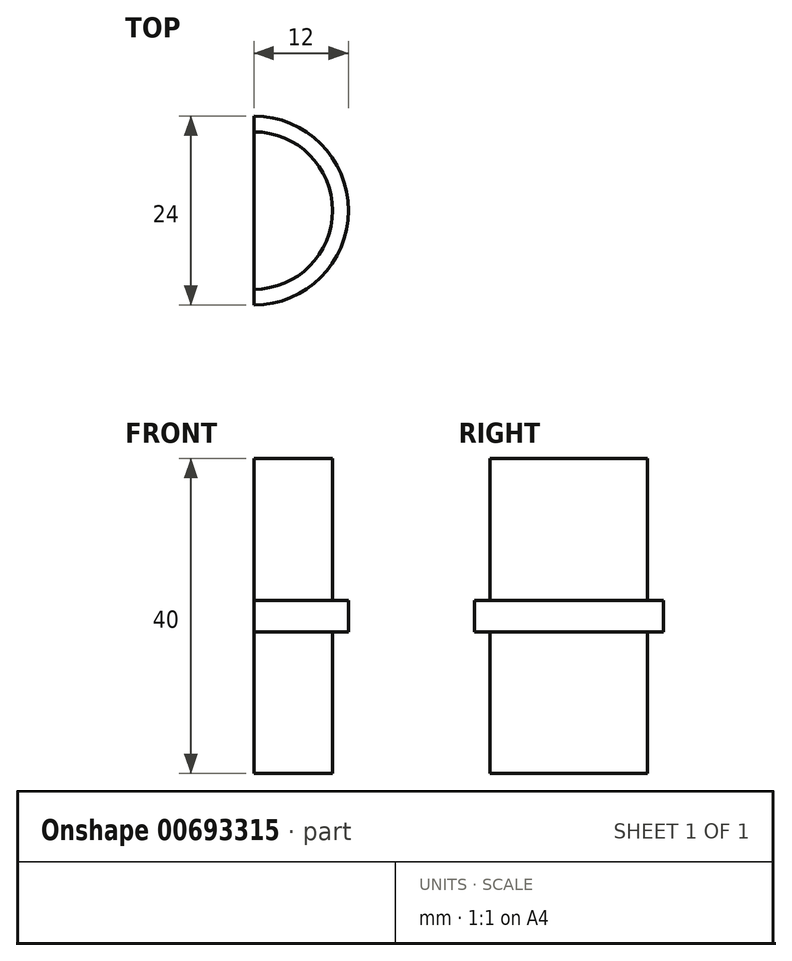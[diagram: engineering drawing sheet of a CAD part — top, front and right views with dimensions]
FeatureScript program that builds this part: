
annotation { "Feature Type Name" : "Feature", "Feature Type Description" : "" }
export const myFeature = defineFeature(function(context is Context, id is Id, definition is map)
    precondition{}
    {
        {
            var Q0;
            Q0=qCreatedBy(makeId("Front.planeOp"),FACE);
            var sketch = newSketch(context, id + "F0", { "sketchPlane" : qUnion([Q0])});
            skLineSegment(sketch, "E0", {"start": v(0, 0) * mm, "end": v(0, 20) * mm});
            skLineSegment(sketch, "E1", {"start": v(0, 20) * mm, "end": v(10, 20) * mm});
            skLineSegment(sketch, "E2", {"start": v(10, 20) * mm, "end": v(10, 0) * mm});
            skLineSegment(sketch, "E3", {"start": v(10, 0) * mm, "end": v(10, -20) * mm});
            skLineSegment(sketch, "E4", {"start": v(10, -20) * mm, "end": v(0, -20) * mm});
            skLineSegment(sketch, "E5", {"start": v(0, -20) * mm, "end": v(0, 0) * mm});
            skLineSegment(sketch, "E6", {"start": v(10, 0) * mm, "end": v(12, 0) * mm});
            skLineSegment(sketch, "E7", {"start": v(12, 0) * mm, "end": v(12, 2) * mm});
            skLineSegment(sketch, "E8", {"start": v(12, 2) * mm, "end": v(10, 2) * mm});
            skLineSegment(sketch, "E9", {"start": v(12, 0) * mm, "end": v(12, -2) * mm});
            skLineSegment(sketch, "E10", {"start": v(12, -2) * mm, "end": v(10, -2) * mm});
            skSolve(sketch);
        }
        {
            var Q0;
            Q0=makeQuery(id+"F0.imprint","IMPRINT",FACE,{"disambiguationData":[TD([[makeQuery(id+"F0.imprint","IMPRINT",EDGE,{"derivedFrom":sQuery(id+"F0.wireOp",EDGE,"E0")}),-1.0]])]});
            var Q1;
            {var subQ0=sQuery(id+"F0.wireOp",EDGE,"E6");Q1=makeQuery(id+"F0.imprint","IMPRINT",FACE,{"disambiguationData":[TD([[makeQuery(id+"F0.imprint","IMPRINT",EDGE,{"derivedFrom":subQ0}),-1.0]])]});}
            var Q2;
            {var subQ0=sQuery(id+"F0.wireOp",EDGE,"E6");Q2=makeQuery(id+"F0.imprint","IMPRINT",FACE,{"disambiguationData":[TD([[makeQuery(id+"F0.imprint","IMPRINT",EDGE,{"derivedFrom":subQ0}),1.0]])]});}
            var Q3;
            Q3=sQuery(id+"F0.wireOp",EDGE,"E0");
            revolve(context, id + "F1", {"entities" : qUnion([Q0, Q1, Q2]), "axis" : qUnion([Q3]), "revolveType" : RevolveType.SYMMETRIC, "angle" : 180 * degree});
        }
    });
